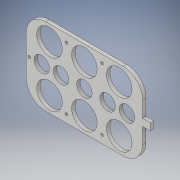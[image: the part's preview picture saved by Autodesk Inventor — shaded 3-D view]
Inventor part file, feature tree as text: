
AUTODESK INVENTOR PART (.ipt)
format: ipt  version: 2017 (Build 210142000, 142)  size: 206,336 bytes
history: native  units: in
note: dims shown in document units (in); Inventor stores cm internally (conversion verified against a paired STEP export)
features: fillet x4, extrude x2, sketch x2
ambient origin geometry x8: Origin, YZ Plane, XZ Plane, XY Plane, X Axis, Y Axis, Z Axis, Center Point
bodies: Body1 (feature_tree)
feature tree (8):
  extrude  "Extrusion5"  Depth=3.937in
  extrude  "Extrusion6"  Depth=0.9843in
  fillet  "Fillet9"  Radius=1.2992in
  fillet  "Fillet10"  Radius=1.2992in
  fillet  "Fillet11"  Radius=1.2992in
  fillet  "Fillet12"  Radius=1.2992in
  sketch  "Sketch1"  dims[d0=5.9055in d1=3.937in]
  sketch  "Sketch4"  dims[d2=1.2992in d3=1.2992in d5=1.2992in d6=1.2992in d8=1.2992in d9=1.2992in d10=0.7874in d11=0.7874in d12=0.7874in d13=1.1811in d14=1.1811in d15=2.9528in d16=1.1811in d17=2.9528in d18=1.1811in d19=0.7874in d20=0.7874in d21=0.7874in d22=0.7874in d23=0.7874in d25=0.7874in d26=0.7874in d27=0.7874in d28=0.7874in d29=0.7874in d30=0.9843in d31=0.9843in d32=1.9685in d33=1.9685in d34=1.9685in d35=1.9685in d36=1.9685in d37=2.9528in d56=0.1378in d57=0.1378in d58=0.1378in d59=0.1378in d60=0.3937in d61=0.3937in d62=0.3937in d63=0.3937in d64=2.0472in d65=2.0472in d66=2.0472in d67=2.0472in d74=0.1378in d75=0.1575in d76=1.9685in d77=0.1772in d78=0.0in d79=0.3543in d80=1.7913in d81=0.3937in d82=0.0in d83=0.9843in d84=0.9843in d85=0.9843in d86=0.9843in]
